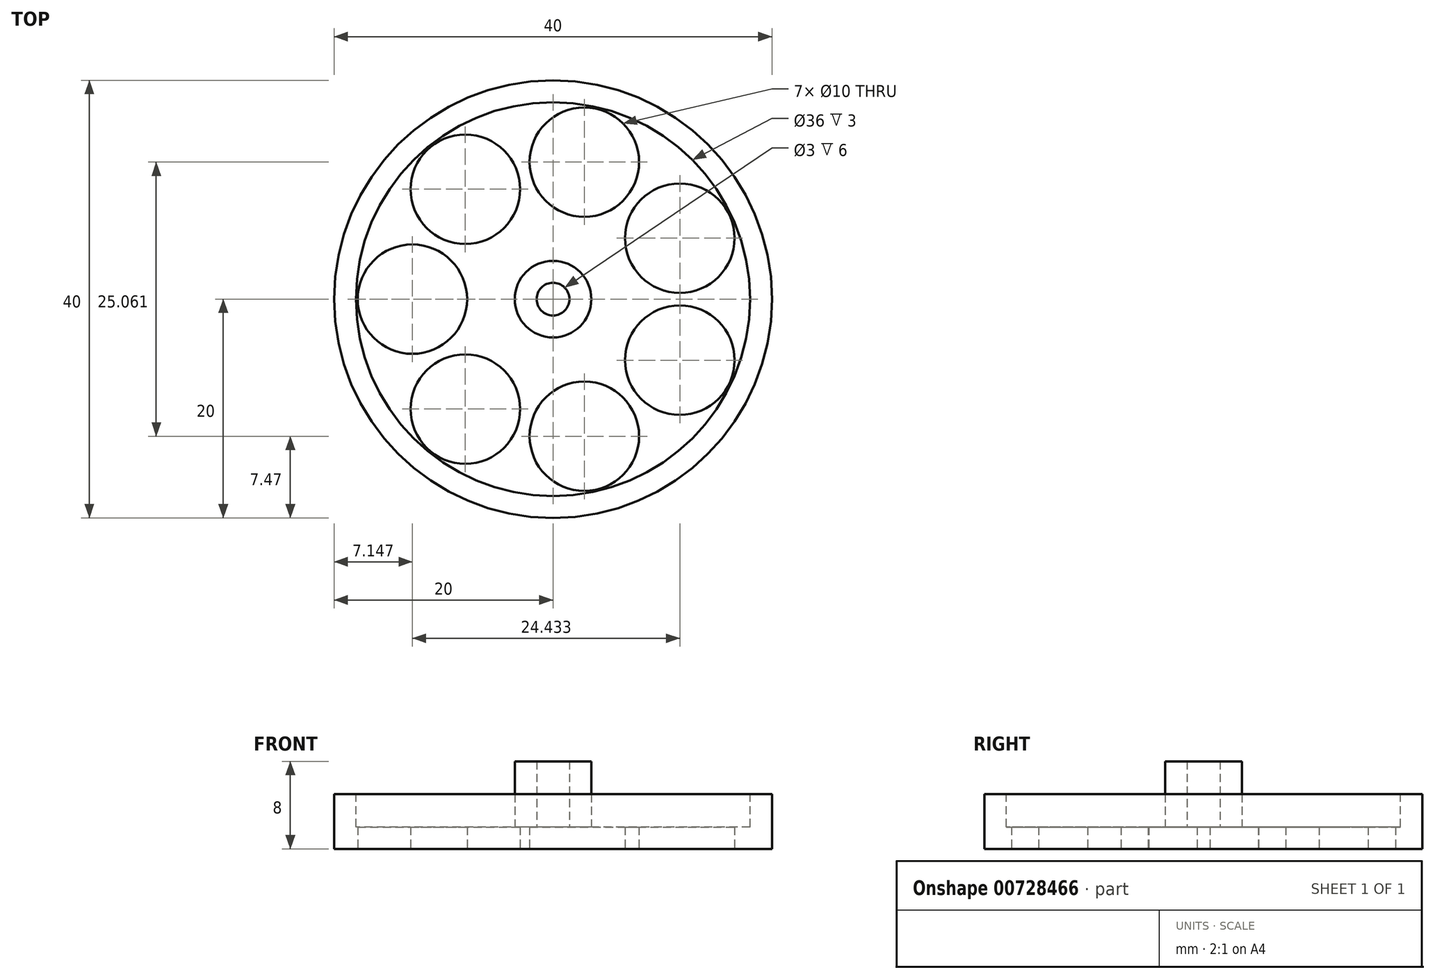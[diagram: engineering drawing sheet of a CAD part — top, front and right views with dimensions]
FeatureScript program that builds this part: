
annotation { "Feature Type Name" : "Feature", "Feature Type Description" : "" }
export const myFeature = defineFeature(function(context is Context, id is Id, definition is map)
    precondition{}
    {
        {
            var Q0;
            Q0=qCreatedBy(makeId("Top.planeOp"),FACE);
            var sketch = newSketch(context, id + "F0", { "sketchPlane" : qUnion([Q0])});
            skCircle(sketch, "E0", {"center": v(0, 0) * mm, "radius": 20 * mm});
            skSolve(sketch);
        }
        {
            var Q0;
            Q0=makeQuery(id+"F0.imprint","IMPRINT",FACE,{"disambiguationData":[TD([[makeQuery(id+"F0.imprint","IMPRINT",EDGE,{"derivedFrom":sQuery(id+"F0.wireOp",EDGE,"E0")}),1.0]])]});
            extrude(context, id + "F1", {"entities" : qUnion([Q0]), "depth" : 5 * mm, "offsetDistance" : 25 * mm});
        }
        {
            var Q0;
            Q0=makeQuery(id+"F1.opExtrude","CAP_FACE",FACE,{"disambiguationData":[OSD([sQuery(id+"F0.wireOp",EDGE,"E0")])],"isStart":false});
            var sketch = newSketch(context, id + "F2", { "sketchPlane" : qUnion([Q0])});
            skCircle(sketch, "E1", {"center": v(0, 0) * mm, "radius": 18 * mm});
            skSolve(sketch);
        }
        {
            var Q0;
            Q0=makeQuery(id+"F2.imprint","IMPRINT",FACE,{"disambiguationData":[TD([[makeQuery(id+"F2.imprint","IMPRINT",EDGE,{"derivedFrom":sQuery(id+"F2.wireOp",EDGE,"E1")}),1.0]])]});
            extrude(context, id + "F3", {"entities" : qUnion([Q0]), "operationType" : NewBodyOperationType.REMOVE, "oppositeDirection" : true, "depth" : 3 * mm, "offsetDistance" : 25 * mm});
        }
        {
            var Q0;
            Q0=makeQuery(id+"F3.boolean.opBoolean","COPY",FACE,{"derivedFrom":makeQuery(id+"F3.opExtrude","CAP_FACE",FACE,{"disambiguationData":[OSD([sQuery(id+"F2.wireOp",EDGE,"E1")])],"isStart":false})});
            var sketch = newSketch(context, id + "F4", { "sketchPlane" : qUnion([Q0])});
            skCircle(sketch, "E2", {"center": v(0, 0) * mm, "radius": 1.5 * mm});
            skCircle(sketch, "E3", {"center": v(0, 0) * mm, "radius": 3.5 * mm});
            skSolve(sketch);
        }
        {
            var Q0;
            Q0=makeQuery(id+"F4.imprint","IMPRINT",FACE,{"disambiguationData":[TD([[makeQuery(id+"F4.imprint","IMPRINT",EDGE,{"derivedFrom":sQuery(id+"F4.wireOp",EDGE,"E2")}),-1.0]])]});
            extrude(context, id + "F5", {"entities" : qUnion([Q0]), "operationType" : NewBodyOperationType.ADD, "depth" : 6 * mm, "offsetDistance" : 25 * mm});
        }
        {
            var Q0;
            Q0=makeQuery(id+"F1.opExtrude","CAP_FACE",FACE,{"disambiguationData":[OSD([sQuery(id+"F0.wireOp",EDGE,"E0")])],"isStart":true});
            var sketch = newSketch(context, id + "F6", { "sketchPlane" : qUnion([Q0])});
            skCircle(sketch, "E4", {"center": v(-12.85, 0) * mm, "radius": 5 * mm});
            skCircle(sketch, "E5.1.0", {"center": v(-8.01, -10.05) * mm, "radius": 5 * mm});
            skCircle(sketch, "E5.2.0", {"center": v(2.86, -12.53) * mm, "radius": 5 * mm});
            skCircle(sketch, "E5.3.0", {"center": v(11.58, -5.58) * mm, "radius": 5 * mm});
            skCircle(sketch, "E5.4.0", {"center": v(11.58, 5.58) * mm, "radius": 5 * mm});
            skPoint(sketch, "E5.center", {"position": v(0, 0) * mm});
            skCircle(sketch, "E6.1.5.0", {"center": v(2.86, 12.53) * mm, "radius": 5 * mm});
            skCircle(sketch, "E6.1.6.0", {"center": v(-8.01, 10.05) * mm, "radius": 5 * mm});
            skSolve(sketch);
        }
        {
            var Q0;
            Q0 = qSketchRegion(id + "F6", true);
            extrude(context, id + "F7", {"entities" : qUnion([Q0]), "operationType" : NewBodyOperationType.REMOVE, "oppositeDirection" : true, "depth" : 2 * mm, "offsetDistance" : 25 * mm});
        }
    });
